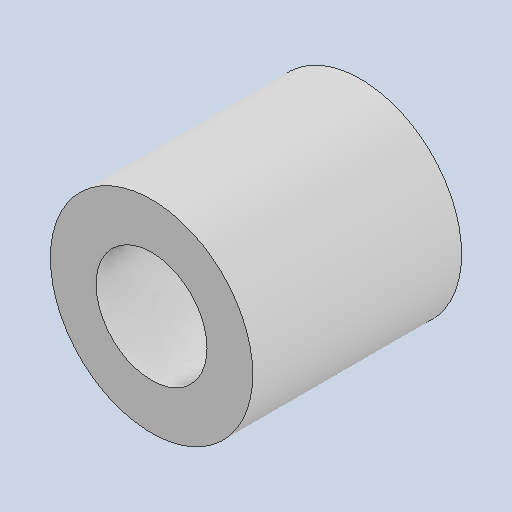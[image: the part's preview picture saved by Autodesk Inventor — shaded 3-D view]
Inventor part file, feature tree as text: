
AUTODESK INVENTOR PART (.ipt)
format: ipt  version: 2024 (Build 280153000, 153)  size: 97,280 bytes
history: native  units: in
note: dims shown in document units (in); Inventor stores cm internally (conversion verified against a paired STEP export)
features: other x3, sketch x1
ambient origin geometry x8: Origin, YZ Plane, XZ Plane, XY Plane, X Axis, Y Axis, Z Axis, Center Point
bodies: Solid1 (feature_tree)
feature tree (4):
  other  "Part1.ipt"
  other  "Solid1::Part1.ipt"
  other  "TaggingFeature1"
  sketch  "Sketch1"  dims[d0=0.3937in]
